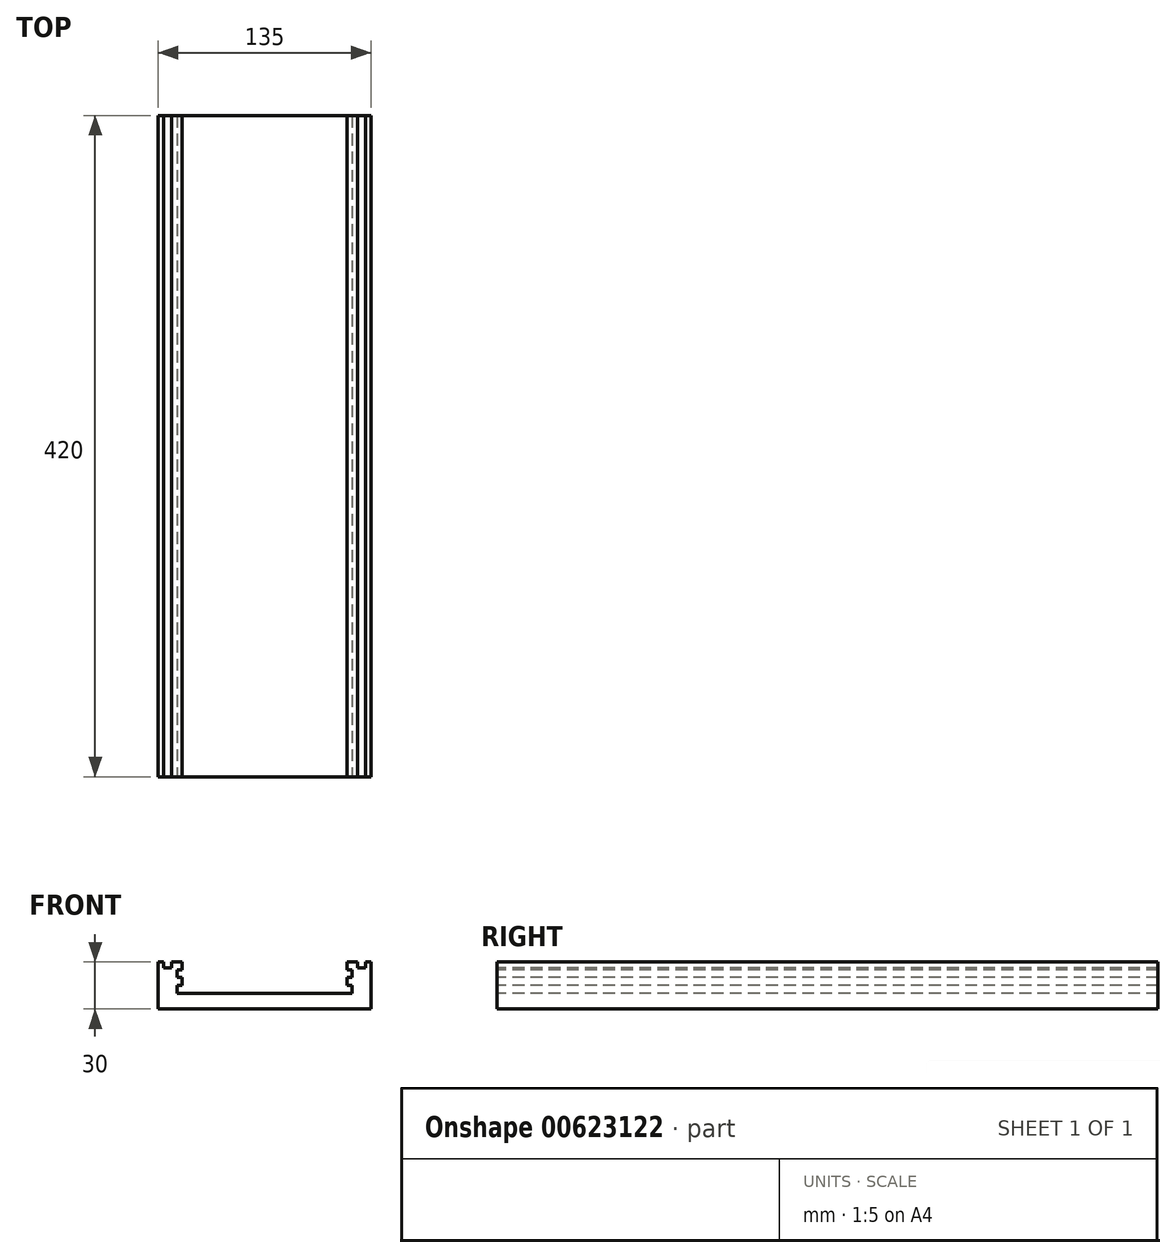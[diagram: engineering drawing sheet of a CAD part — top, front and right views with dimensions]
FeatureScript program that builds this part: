
annotation { "Feature Type Name" : "Feature", "Feature Type Description" : "" }
export const myFeature = defineFeature(function(context is Context, id is Id, definition is map)
    precondition{}
    {
        {
            var Q0;
            Q0=qCreatedBy(makeId("Front.planeOp"),FACE);
            var sketch = newSketch(context, id + "F0", { "sketchPlane" : qUnion([Q0])});
            skLineSegment(sketch, "E0.bottom", {"start": v(-67.5, 0) * mm, "end": v(67.5, 0) * mm});
            skLineSegment(sketch, "E0.top", {"start": v(-67.5, 30) * mm, "end": v(67.5, 30) * mm});
            skLineSegment(sketch, "E0.left", {"start": v(-67.5, 0) * mm, "end": v(-67.5, 30) * mm});
            skLineSegment(sketch, "E0.right", {"start": v(67.5, 0) * mm, "end": v(67.5, 30) * mm});
            skSolve(sketch);
        }
        {
            var Q0;
            Q0 = qSketchRegion(id + "F0", true);
            extrude(context, id + "F1", {"entities" : qUnion([Q0]), "depth" : 420 * mm, "offsetDistance" : 25 * mm});
        }
        {
            var Q0;
            Q0=makeQuery(id+"F1.opExtrude","CAP_FACE",FACE,{"disambiguationData":[OSD([sQuery(id+"F0.wireOp",EDGE,"E0.bottom"),sQuery(id+"F0.wireOp",EDGE,"E0.top"),sQuery(id+"F0.wireOp",EDGE,"E0.left"),sQuery(id+"F0.wireOp",EDGE,"E0.right")])],"isStart":false});
            var sketch = newSketch(context, id + "F2", { "sketchPlane" : qUnion([Q0])});
            skLineSegment(sketch, "E1", {"start": v(-52.5, 30) * mm, "end": v(-52.5, 25) * mm});
            skLineSegment(sketch, "E2", {"start": v(-52.5, 25) * mm, "end": v(-55.5, 25) * mm});
            skLineSegment(sketch, "E3", {"start": v(-55.5, 25) * mm, "end": v(-55.5, 20) * mm});
            skLineSegment(sketch, "E4", {"start": v(-55.5, 20) * mm, "end": v(-52.5, 20) * mm});
            skLineSegment(sketch, "E5", {"start": v(-52.5, 20) * mm, "end": v(-52.5, 15) * mm});
            skLineSegment(sketch, "E6", {"start": v(-52.5, 15) * mm, "end": v(-55.5, 15) * mm});
            skLineSegment(sketch, "E7", {"start": v(-55.5, 15) * mm, "end": v(-55.5, 10) * mm});
            skLineSegment(sketch, "E8", {"start": v(-55.5, 10) * mm, "end": v(0, 10) * mm});
            skLineSegment(sketch, "E9", {"start": v(-52.5, 30) * mm, "end": v(0, 30) * mm});
            skLineSegment(sketch, "E10", {"start": v(0, 41.6) * mm, "end": v(0, -14.07) * mm, "construction": true});
            skLineSegment(sketch, "E11.MirrorCS", {"start": v(55.5, 15) * mm, "end": v(55.5, 10) * mm});
            skLineSegment(sketch, "E12.MirrorCS", {"start": v(52.5, 15) * mm, "end": v(55.5, 15) * mm});
            skLineSegment(sketch, "E13.MirrorCS", {"start": v(52.5, 20) * mm, "end": v(52.5, 15) * mm});
            skLineSegment(sketch, "E14.MirrorCS", {"start": v(55.5, 20) * mm, "end": v(52.5, 20) * mm});
            skLineSegment(sketch, "E15.MirrorCS", {"start": v(55.5, 25) * mm, "end": v(55.5, 20) * mm});
            skLineSegment(sketch, "E16.MirrorCS", {"start": v(52.5, 25) * mm, "end": v(55.5, 25) * mm});
            skLineSegment(sketch, "E17.MirrorCS", {"start": v(52.5, 30) * mm, "end": v(52.5, 25) * mm});
            skLineSegment(sketch, "E18.MirrorCS", {"start": v(52.5, 30) * mm, "end": v(0, 30) * mm});
            skLineSegment(sketch, "E19.MirrorCS", {"start": v(55.5, 10) * mm, "end": v(0, 10) * mm});
            skSolve(sketch);
        }
        {
            var Q0;
            Q0=makeQuery(id+"F2.imprint","IMPRINT",FACE,{"disambiguationData":[TD([[makeQuery(id+"F2.imprint","IMPRINT",EDGE,{"derivedFrom":sQuery(id+"F2.wireOp",EDGE,"E1")}),1.0]])]});
            extrude(context, id + "F3", {"entities" : qUnion([Q0]), "operationType" : NewBodyOperationType.REMOVE, "oppositeDirection" : true, "depth" : 420 * mm, "offsetDistance" : 25 * mm});
        }
        {
            var Q0;
            {var subQ0=sQuery(id+"F0.wireOp",EDGE,"E0.right");var subQ2=sQuery(id+"F0.wireOp",EDGE,"E0.top");Q0=makeQuery(id+"F3.boolean.opBoolean","SPLIT",FACE,{"disambiguationData":[TD([makeQuery(id+"F1.opExtrude","SWEPT_FACE",FACE,{"disambiguationData":[OSD([subQ0])]})])],"derivedFrom":makeQuery(id+"F1.opExtrude","SWEPT_FACE",FACE,{"disambiguationData":[OSD([subQ2])]})});}
            var sketch = newSketch(context, id + "F4", { "sketchPlane" : qUnion([Q0])});
            skLineSegment(sketch, "E20.bottom", {"start": v(-64, 0) * mm, "end": v(-59, 0) * mm});
            skLineSegment(sketch, "E20.top", {"start": v(-64, -420) * mm, "end": v(-59, -420) * mm});
            skLineSegment(sketch, "E20.left", {"start": v(-64, 0) * mm, "end": v(-64, -420) * mm});
            skLineSegment(sketch, "E20.right", {"start": v(-59, 0) * mm, "end": v(-59, -420) * mm});
            skPoint(sketch, "E21.MirrorP", {"position": v(-61.5, 0) * mm});
            skLineSegment(sketch, "E22.MirrorCS", {"start": v(64, -420) * mm, "end": v(59, -420) * mm});
            skLineSegment(sketch, "E23.MirrorCS", {"start": v(64, 0) * mm, "end": v(59, 0) * mm});
            skLineSegment(sketch, "E24.MirrorCS", {"start": v(59, 0) * mm, "end": v(59, -420) * mm});
            skLineSegment(sketch, "E25.MirrorCS", {"start": v(64, 0) * mm, "end": v(64, -420) * mm});
            skSolve(sketch);
        }
        {
            var Q0;
            Q0 = qSketchRegion(id + "F4", true);
            extrude(context, id + "F5", {"entities" : qUnion([Q0]), "operationType" : NewBodyOperationType.REMOVE, "oppositeDirection" : true, "depth" : 4 * mm, "offsetDistance" : 25 * mm});
        }
    });
